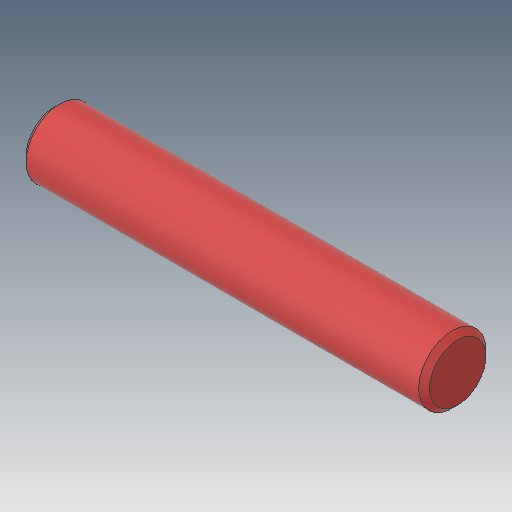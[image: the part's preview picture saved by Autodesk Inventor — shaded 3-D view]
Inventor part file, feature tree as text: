
AUTODESK INVENTOR PART (.ipt)
format: ipt  version: 2019.4 (Build 234330000, 330)  size: 100,352 bytes
history: native  units: mm
features: other x1, extrude x1, chamfer x1, sketch x1
ambient origin geometry x8: Origin, YZ Plane, XZ Plane, XY Plane, X Axis, Y Axis, Z Axis, Center Point
bodies: Body1 (feature_tree)
feature tree (4):
  other  "ソリッド1"
  extrude  "押し出し1"  Depth=2.5mm
  chamfer  "面取り1"  Distance=15.0mm
  sketch  "スケッチ1"
